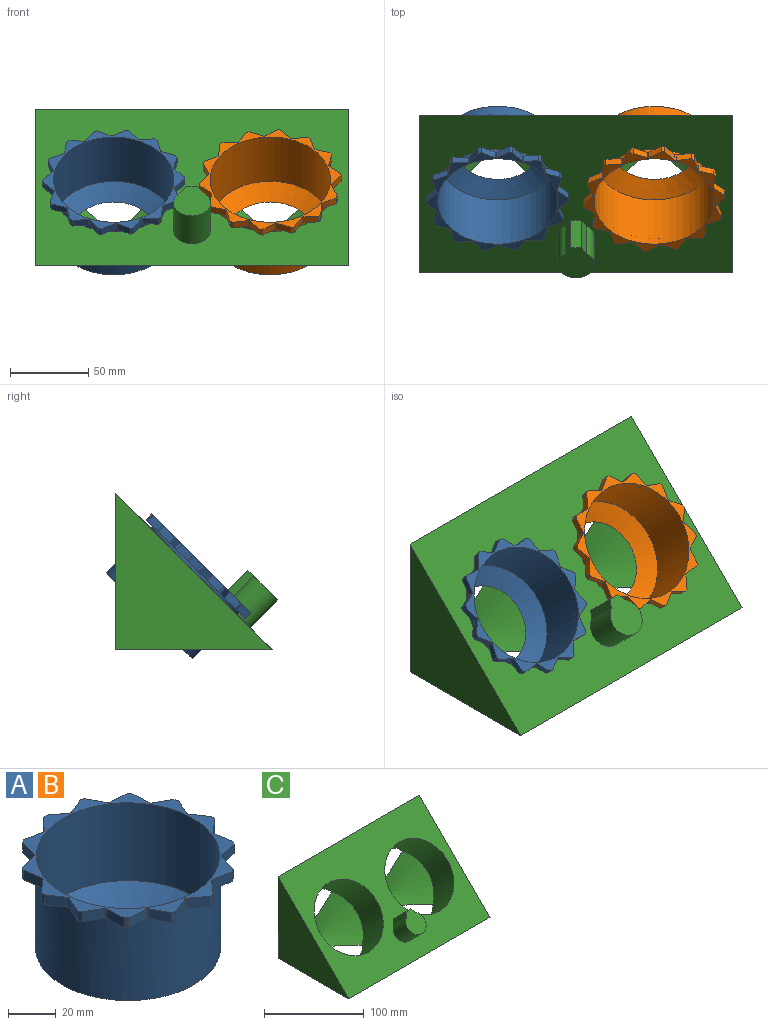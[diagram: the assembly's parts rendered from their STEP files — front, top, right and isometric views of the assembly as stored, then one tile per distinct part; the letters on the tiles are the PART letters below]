
ASSEMBLY  parts=3 mates=2
PART A: 62 faces, bbox 90x90.4x47 mm
  f0: cylinder r=39.5mm len=5mm, axis (0,0,-1), area 3.7mm2, adj f17,f18,f51,f54
  f1: cylinder r=39.5mm len=5mm, axis (0,0,-1), area 3.7mm2, adj f17,f18,f53,f57
  f2: cylinder r=39.5mm len=5mm, axis (0,0,-1), area 3.7mm2, adj f17,f18,f21,f55
  f3: cylinder r=39.5mm len=5mm, axis (0,0,-1), area 3.7mm2, adj f17,f18,f20,f24
  f4: cylinder r=39.5mm len=5mm, axis (0,0,-1), area 3.7mm2, adj f17,f18,f23,f27
  f5: cylinder r=39.5mm len=5mm, axis (0,0,-1), area 3.7mm2, adj f17,f18,f26,f30
  f6: cylinder r=39.5mm len=5mm, axis (0,0,-1), area 3.7mm2, adj f17,f18,f29,f33
  f7: cylinder r=39.5mm len=5mm, axis (0,0,-1), area 3.7mm2, adj f17,f18,f32,f36
  f8: cylinder r=39.5mm len=5mm, axis (0,0,-1), area 3.7mm2, adj f17,f18,f35,f39
  f9: cylinder r=39.5mm len=5mm, axis (0,0,-1), area 3.7mm2, adj f17,f18,f38,f42
  f10: cylinder r=39.5mm len=5mm, axis (0,0,-1), area 3.7mm2, adj f17,f18,f41,f45
  f11: cylinder r=39.5mm len=5mm, axis (0,0,-1), area 3.7mm2, adj f17,f18,f44,f48
  f12: cylinder r=39.5mm len=5mm, axis (0,0,-1), area 3.7mm2, adj f16,f17,f18,f47
  f13: cylinder r=39.5mm len=5mm, axis (0,0,-1), area 3.7mm2, adj f14,f17,f18,f50
  f14: plane 8.02x5.98mm, normal (0.6,0.8,0), area 50mm2, adj f13,f15,f17,f18
  f15: plane 5x2mm, normal (-0.13,0.99,0), area 10.1mm2, adj f14,f16,f17,f18
  f16: plane 7.37x6.76mm, normal (-0.74,0.68,0), area 50mm2, adj f12,f15,f17,f18
  f17: plane 90.42x90.04mm, normal (0,0,1), area 987.1mm2, adj f0,f1,f2,f3,f4,f5,f6,f7
  f18: plane 90.42x90.04mm, normal (0,0,-1), area 865.4mm2, adj f0,f1,f2,f3,f4,f5,f6,f7
  f19: plane 5x2.01mm, normal (1,-0.09,0), area 10.1mm2, adj f17,f18,f20,f21
  f20: plane 7.61x6.49mm, normal (0.65,-0.76,0), area 50mm2, adj f3,f17,f18,f19
  f21: plane 8.23x5.68mm, normal (0.82,0.57,0), area 50mm2, adj f2,f17,f18,f19
  f22: plane 5x1.73mm, normal (0.86,-0.51,0), area 10.1mm2, adj f17,f18,f23,f24
  f23: plane 9.67x5mm, normal (0.25,-0.97,0), area 50mm2, adj f4,f17,f18,f22
  f24: plane 9.88x5mm, normal (0.99,0.15,0), area 50mm2, adj f3,f17,f18,f22
  f25: plane 5x1.68mm, normal (0.55,-0.83,0), area 10.1mm2, adj f17,f18,f26,f27
  f26: plane 9.82x5mm, normal (-0.19,-0.98,0), area 50mm2, adj f5,f17,f18,f25
  f27: plane 9.57x5mm, normal (0.96,-0.29,0), area 50mm2, adj f4,f17,f18,f25
  f28: plane 5x2mm, normal (0.13,-0.99,0), area 10.1mm2, adj f17,f18,f29,f30
  f29: plane 8.02x5.98mm, normal (-0.6,-0.8,0), area 50mm2, adj f6,f17,f18,f28
  f30: plane 7.37x6.76mm, normal (0.74,-0.68,0), area 50mm2, adj f5,f17,f18,f28
  f31: plane 5x1.92mm, normal (-0.31,-0.95,0), area 10.1mm2, adj f17,f18,f32,f33
  f32: plane 8.86x5mm, normal (-0.89,-0.46,0), area 50mm2, adj f7,f17,f18,f31
  f33: plane 9.29x5mm, normal (0.37,-0.93,0), area 50mm2, adj f6,f17,f18,f31
  f34: plane 5x1.46mm, normal (-0.69,-0.72,0), area 10.1mm2, adj f17,f18,f35,f36
  f35: plane 9.99x5mm, normal (-1,-0.03,0), area 50mm2, adj f8,f17,f18,f34
  f36: plane 9.98x5mm, normal (-0.07,-1,0), area 50mm2, adj f7,f17,f18,f34
  f37: plane 5x1.89mm, normal (-0.94,-0.35,0), area 10.1mm2, adj f17,f18,f38,f39
  f38: plane 9.15x5mm, normal (-0.91,0.4,0), area 50mm2, adj f9,f17,f18,f37
  f39: plane 8.69x5mm, normal (-0.5,-0.87,0), area 50mm2, adj f8,f17,f18,f37
  f40: plane 5x2.01mm, normal (-1,0.09,0), area 10.1mm2, adj f17,f18,f41,f42
  f41: plane 7.61x6.49mm, normal (-0.65,0.76,0), area 50mm2, adj f10,f17,f18,f40
  f42: plane 8.23x5.68mm, normal (-0.82,-0.57,0), area 50mm2, adj f9,f17,f18,f40
  f43: plane 5x1.73mm, normal (-0.86,0.51,0), area 10.1mm2, adj f17,f18,f44,f45
  f44: plane 9.67x5mm, normal (-0.25,0.97,0), area 50mm2, adj f11,f17,f18,f43
  f45: plane 9.88x5mm, normal (-0.99,-0.15,0), area 50mm2, adj f10,f17,f18,f43
  f46: plane 5x1.68mm, normal (-0.55,0.83,0), area 10.1mm2, adj f17,f18,f47,f48
  f47: plane 9.82x5mm, normal (0.19,0.98,0), area 50mm2, adj f12,f17,f18,f46
  f48: plane 9.57x5mm, normal (-0.96,0.29,0), area 50mm2, adj f11,f17,f18,f46
  f49: plane 5x1.92mm, normal (0.31,0.95,0), area 10.1mm2, adj f17,f18,f50,f51
  f50: plane 9.29x5mm, normal (-0.37,0.93,0), area 50mm2, adj f13,f17,f18,f49
  f51: plane 8.86x5mm, normal (0.89,0.46,0), area 50mm2, adj f0,f17,f18,f49
  f52: plane 5x1.46mm, normal (0.69,0.72,0), area 10.1mm2, adj f17,f18,f53,f54
  f53: plane 9.99x5mm, normal (1,0.03,0), area 50mm2, adj f1,f17,f18,f52
  f54: plane 9.98x5mm, normal (0.07,1,0), area 50mm2, adj f0,f17,f18,f52
  f55: plane 9.15x5mm, normal (0.91,-0.4,0), area 50mm2, adj f2,f17,f18,f56
  f56: plane 5x1.89mm, normal (0.94,0.35,0), area 10.1mm2, adj f17,f18,f55,f57
  f57: plane 8.69x5mm, normal (0.5,0.87,0), area 50mm2, adj f1,f17,f18,f56
  f58: cylinder r=39mm len=78mm, axis (0,0,1), area 10291.9mm2, adj f18,f59
  f59: plane 78x78mm, normal (0,0,-1), area 2513.5mm2, adj f58,f60
  f60: cone r=0mm half-angle=59deg, axis (0,0,1), area 2790.3mm2, adj f59,f61
  f61: cylinder r=38.5mm len=77mm, axis (0,0,1), area 9676.1mm2, adj f17,f60
PART B: same geometry as A
PART C: 14 faces, bbox 200x110.2x106.6 mm
  f0: plane 200x100mm, normal (0,0,-1), area 17883.1mm2, adj f1,f2,f3,f4,f5,f6,f7,f8
  f1: plane 200x100mm, normal (0,1,0), area 17883.3mm2, adj f0,f2,f3,f4,f5,f6,f7,f8
  f2: plane 200x100mm, normal (0,-0.71,0.71), area 17755.7mm2, adj f0,f1,f3,f4,f6,f8,f9,f10
  f3: plane 100x100mm, normal (1,0,0), area 5000mm2, adj f0,f1,f2
  f4: plane 100x100mm, normal (-1,0,0), area 5000mm2, adj f0,f1,f2
  f5: cone r=0mm half-angle=59deg, axis (0,-0.71,0.71), area 4117.6mm2, adj f0,f1,f6
  f6: cylinder r=40mm len=84.85mm, axis (0,-0.71,0.71), area 9369.7mm2, adj f0,f1,f2,f5
  f7: cone r=0mm half-angle=59deg, axis (0,-0.71,0.71), area 4117.6mm2, adj f0,f1,f8
  f8: cylinder r=40mm len=84.85mm, axis (0,-0.71,0.71), area 9369.7mm2, adj f0,f1,f2,f7
  f9: plane 17.68x17.68mm, normal (0,0.71,0.71), area 172.5mm2, adj f2,f10,f12,f13
  f10: plane 21.4x21.4mm, normal (-0.87,0.35,0.35), area 150.9mm2, adj f2,f9,f11,f13
  f11: cylinder r=11.83mm len=33.08mm, axis (0,0.71,-0.71), area 1520.4mm2, adj f2,f10,f12,f13
  f12: plane 21.4x21.4mm, normal (0.87,0.35,0.35), area 150.9mm2, adj f2,f9,f11,f13
  f13: plane 23.67x19.13mm, normal (0,-0.71,0.71), area 475.5mm2, adj f9,f10,f11,f12
PLACE A rot(axis=(0.25,-0.37,0.89),117.8deg) t=(2.17,96.42,136.8)mm
PLACE B rot(axis=(0.36,0.36,-0.86),98.4deg) t=(102.17,96.42,136.8)mm
PLACE C t=(-47.83,147.83,85.39)mm fixed
MATE revolute A.f60 <-> C.f7  axis (0,0.71,-0.71) through (2.17,126.12,107.1)mm
MATE revolute B.f60 <-> C.f5  axis (0,0.71,-0.71) through (102.17,126.12,107.1)mm
